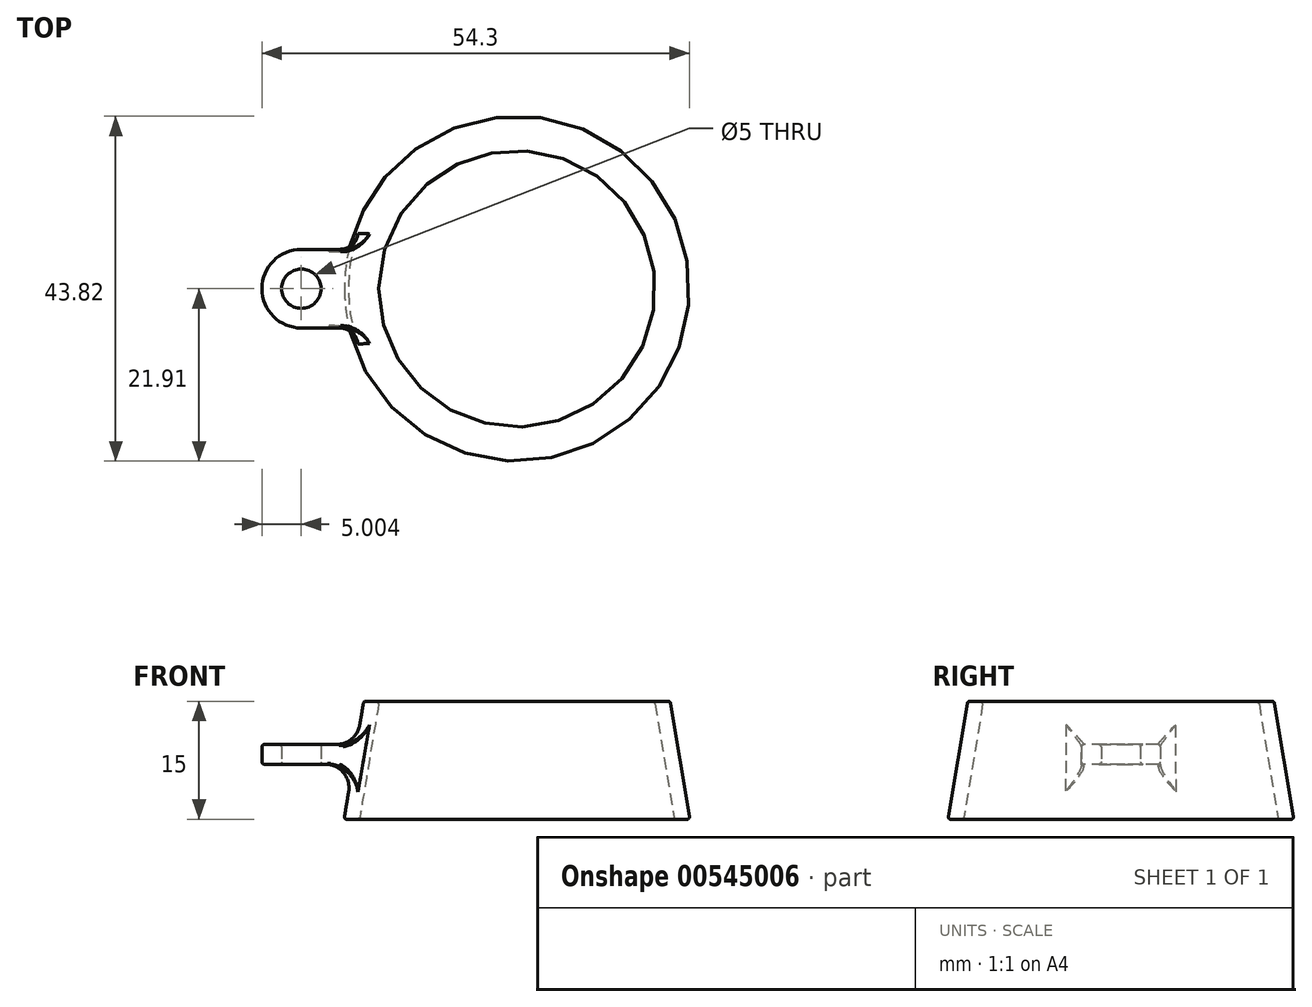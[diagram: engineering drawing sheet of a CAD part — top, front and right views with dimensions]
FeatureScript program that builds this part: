
annotation { "Feature Type Name" : "Feature", "Feature Type Description" : "" }
export const myFeature = defineFeature(function(context is Context, id is Id, definition is map)
    precondition{}
    {
        {
            var Q0;
            Q0=qCreatedBy(makeId("Front.planeOp"),FACE);
            var sketch = newSketch(context, id + "F0", { "sketchPlane" : qUnion([Q0])});
            skLineSegment(sketch, "E0", {"start": v(17.5, 15) * mm, "end": v(20, 0) * mm});
            skLineSegment(sketch, "E1", {"start": v(20, 0) * mm, "end": v(21.96, 0) * mm});
            skLineSegment(sketch, "E2", {"start": v(21.96, 0) * mm, "end": v(19.46, 15) * mm});
            skLineSegment(sketch, "E3", {"start": v(17.5, 15) * mm, "end": v(19.46, 15) * mm});
            skLineSegment(sketch, "E4", {"start": v(0, 0) * mm, "end": v(0, 20) * mm, "construction": true});
            skSolve(sketch);
        }
        {
            var Q0;
            Q0 = qSketchRegion(id + "F0", true);
            var Q1;
            Q1=sQuery(id+"F0.wireOp",EDGE,"E4");
            revolve(context, id + "F1", {"entities" : qUnion([Q0]), "axis" : qUnion([Q1]), "revolveType" : RevolveType.FULL});
        }
        {
            var Q0;
            Q0=qCreatedBy(makeId("Top.planeOp"),FACE);
            cPlane(context, id + "F2", {"entities" : qUnion([Q0]), "cplaneType" : CPlaneType.OFFSET, "offset" : 7 * mm, "width" : 150 * mm, "height" : 150 * mm});
        }
        {
            var Q0;
            Q0=qCreatedBy(id+"F2.planeOp",FACE);
            var sketch = newSketch(context, id + "F3", { "sketchPlane" : qUnion([Q0])});
            skLineSegment(sketch, "E5", {"start": v(-21.39, 5) * mm, "end": v(-27.39, 5) * mm});
            skLineSegment(sketch, "E6", {"start": v(-32.39, 0) * mm, "end": v(-32.39, 0) * mm});
            skLineSegment(sketch, "E7", {"start": v(-27.39, -5) * mm, "end": v(-21.39, -5) * mm});
            skLineSegment(sketch, "E8", {"start": v(-21.39, -5) * mm, "end": v(-21.39, 5) * mm});
            skPoint(sketch, "E9.visualSharp", {"position": v(-32.39, 5) * mm});
            skArc(sketch, "E9.filletArc", {"start": v(-27.39, 5) * mm, "mid": v(-30.92, 3.54) * mm, "end": v(-32.39, 0) * mm});
            skPoint(sketch, "E10.visualSharp", {"position": v(-32.39, -5) * mm});
            skArc(sketch, "E10.filletArc", {"start": v(-32.39, 0) * mm, "mid": v(-30.92, -3.54) * mm, "end": v(-27.39, -5) * mm});
            skCircle(sketch, "E11", {"center": v(-27.39, 0) * mm, "radius": 2.5 * mm});
            skLineSegment(sketch, "E12.0", {"start": v(-19.89, -5) * mm, "end": v(-19.89, 5) * mm});
            skLineSegment(sketch, "E13", {"start": v(-21.39, 5) * mm, "end": v(-19.89, 5) * mm});
            skLineSegment(sketch, "E14", {"start": v(-21.39, -5) * mm, "end": v(-19.89, -5) * mm});
            skSolve(sketch);
        }
        {
            var Q0;
            Q0=makeQuery(id+"F3.imprint","IMPRINT",FACE,{"disambiguationData":[TD([[makeQuery(id+"F3.imprint","IMPRINT",EDGE,{"derivedFrom":sQuery(id+"F3.wireOp",EDGE,"E5")}),1.0]])]});
            var Q1;
            Q1=makeQuery(id+"F3.imprint","IMPRINT",FACE,{"disambiguationData":[TD([[makeQuery(id+"F3.imprint","IMPRINT",EDGE,{"derivedFrom":sQuery(id+"F3.wireOp",EDGE,"E8")}),-1.0]])]});
            extrude(context, id + "F4", {"entities" : qUnion([Q0, Q1]), "operationType" : NewBodyOperationType.ADD, "depth" : 2.5 * mm, "offsetDistance" : 25 * mm});
        }
        {
            var Q0;
            Q0=makeQuery(id+"F4.boolean.opBoolean","INTERSECT",EDGE,{"derivedFrom":[makeQuery(id+"F1.opRevolve","SWEPT_FACE",FACE,{"disambiguationData":[OSD([sQuery(id+"F0.wireOp",EDGE,"E2")])]}),makeQuery(id+"F4.opExtrude","CAP_FACE",FACE,{"disambiguationData":[OSD([sQuery(id+"F3.wireOp",EDGE,"E5"),sQuery(id+"F3.wireOp",EDGE,"E7"),sQuery(id+"F3.wireOp",EDGE,"E9.filletArc"),sQuery(id+"F3.wireOp",EDGE,"E10.filletArc"),sQuery(id+"F3.wireOp",EDGE,"E11"),sQuery(id+"F3.wireOp",EDGE,"E12.0"),sQuery(id+"F3.wireOp",EDGE,"E13"),sQuery(id+"F3.wireOp",EDGE,"E14")])],"isStart":true})]});
            var Q1;
            Q1=makeQuery(id+"F4.boolean.opBoolean","INTERSECT",EDGE,{"derivedFrom":[makeQuery(id+"F1.opRevolve","SWEPT_FACE",FACE,{"disambiguationData":[OSD([sQuery(id+"F0.wireOp",EDGE,"E2")])]}),makeQuery(id+"F4.opExtrude","CAP_FACE",FACE,{"disambiguationData":[OSD([sQuery(id+"F3.wireOp",EDGE,"E5"),sQuery(id+"F3.wireOp",EDGE,"E7"),sQuery(id+"F3.wireOp",EDGE,"E9.filletArc"),sQuery(id+"F3.wireOp",EDGE,"E10.filletArc"),sQuery(id+"F3.wireOp",EDGE,"E11"),sQuery(id+"F3.wireOp",EDGE,"E12.0"),sQuery(id+"F3.wireOp",EDGE,"E13"),sQuery(id+"F3.wireOp",EDGE,"E14")])],"isStart":false})]});
            var Q2;
            Q2=makeQuery(id+"F4.boolean.opBoolean","INTERSECT",EDGE,{"derivedFrom":[makeQuery(id+"F1.opRevolve","SWEPT_FACE",FACE,{"disambiguationData":[OSD([sQuery(id+"F0.wireOp",EDGE,"E2")])]}),makeQuery(id+"F4.opExtrude","SWEPT_FACE",FACE,{"disambiguationData":[OSD([sQuery(id+"F3.wireOp",EDGE,"E5"),sQuery(id+"F3.wireOp",EDGE,"E13")])]})]});
            var Q3;
            Q3=makeQuery(id+"F4.boolean.opBoolean","INTERSECT",EDGE,{"derivedFrom":[makeQuery(id+"F1.opRevolve","SWEPT_FACE",FACE,{"disambiguationData":[OSD([sQuery(id+"F0.wireOp",EDGE,"E2")])]}),makeQuery(id+"F4.opExtrude","SWEPT_FACE",FACE,{"disambiguationData":[OSD([sQuery(id+"F3.wireOp",EDGE,"E7"),sQuery(id+"F3.wireOp",EDGE,"E14")])]})]});
            fillet(context, id + "F5", {"entities" : qUnion([Q0, Q1, Q2, Q3]), "radius" : 3 * mm, "tangentPropagation" : true, "allowEdgeOverflow" : false});
        }
        {
            var Q0;
            Q0=makeQuery(id+"F1.opRevolve","SWEPT_EDGE",EDGE,{"disambiguationData":[OSD([sQuery(id+"F0.wireOp",EDGE,"E2"),sQuery(id+"F0.wireOp",EDGE,"E3")])]});
            var Q1;
            Q1=makeQuery(id+"F1.opRevolve","SWEPT_EDGE",EDGE,{"disambiguationData":[OSD([sQuery(id+"F0.wireOp",EDGE,"E0"),sQuery(id+"F0.wireOp",EDGE,"E3")])]});
            var Q2;
            Q2=makeQuery(id+"F1.opRevolve","SWEPT_EDGE",EDGE,{"disambiguationData":[OSD([sQuery(id+"F0.wireOp",EDGE,"E1"),sQuery(id+"F0.wireOp",EDGE,"E2")])]});
            var Q3;
            Q3=makeQuery(id+"F1.opRevolve","SWEPT_EDGE",EDGE,{"disambiguationData":[OSD([sQuery(id+"F0.wireOp",EDGE,"E0"),sQuery(id+"F0.wireOp",EDGE,"E1")])]});
            var Q4;
            Q4=makeQuery(id+"F4.opExtrude","CAP_EDGE",EDGE,{"disambiguationData":[OSD([sQuery(id+"F3.wireOp",EDGE,"E11")])],"isStart":true});
            var Q5;
            Q5=makeQuery(id+"F4.opExtrude","CAP_EDGE",EDGE,{"disambiguationData":[OSD([sQuery(id+"F3.wireOp",EDGE,"E11")])],"isStart":false});
            var Q6;
            Q6=makeQuery(id+"F4.opExtrude","CAP_EDGE",EDGE,{"disambiguationData":[OSD([sQuery(id+"F3.wireOp",EDGE,"E9.filletArc"),sQuery(id+"F3.wireOp",EDGE,"E10.filletArc")])],"isStart":false});
            var Q7;
            Q7=makeQuery(id+"F4.opExtrude","CAP_EDGE",EDGE,{"disambiguationData":[OSD([sQuery(id+"F3.wireOp",EDGE,"E9.filletArc"),sQuery(id+"F3.wireOp",EDGE,"E10.filletArc")])],"isStart":true});
            fillet(context, id + "F6", {"entities" : qUnion([Q0, Q1, Q2, Q3, Q4, Q5, Q6, Q7]), "radius" : 0.3 * mm, "tangentPropagation" : true, "allowEdgeOverflow" : false});
        }
    });
